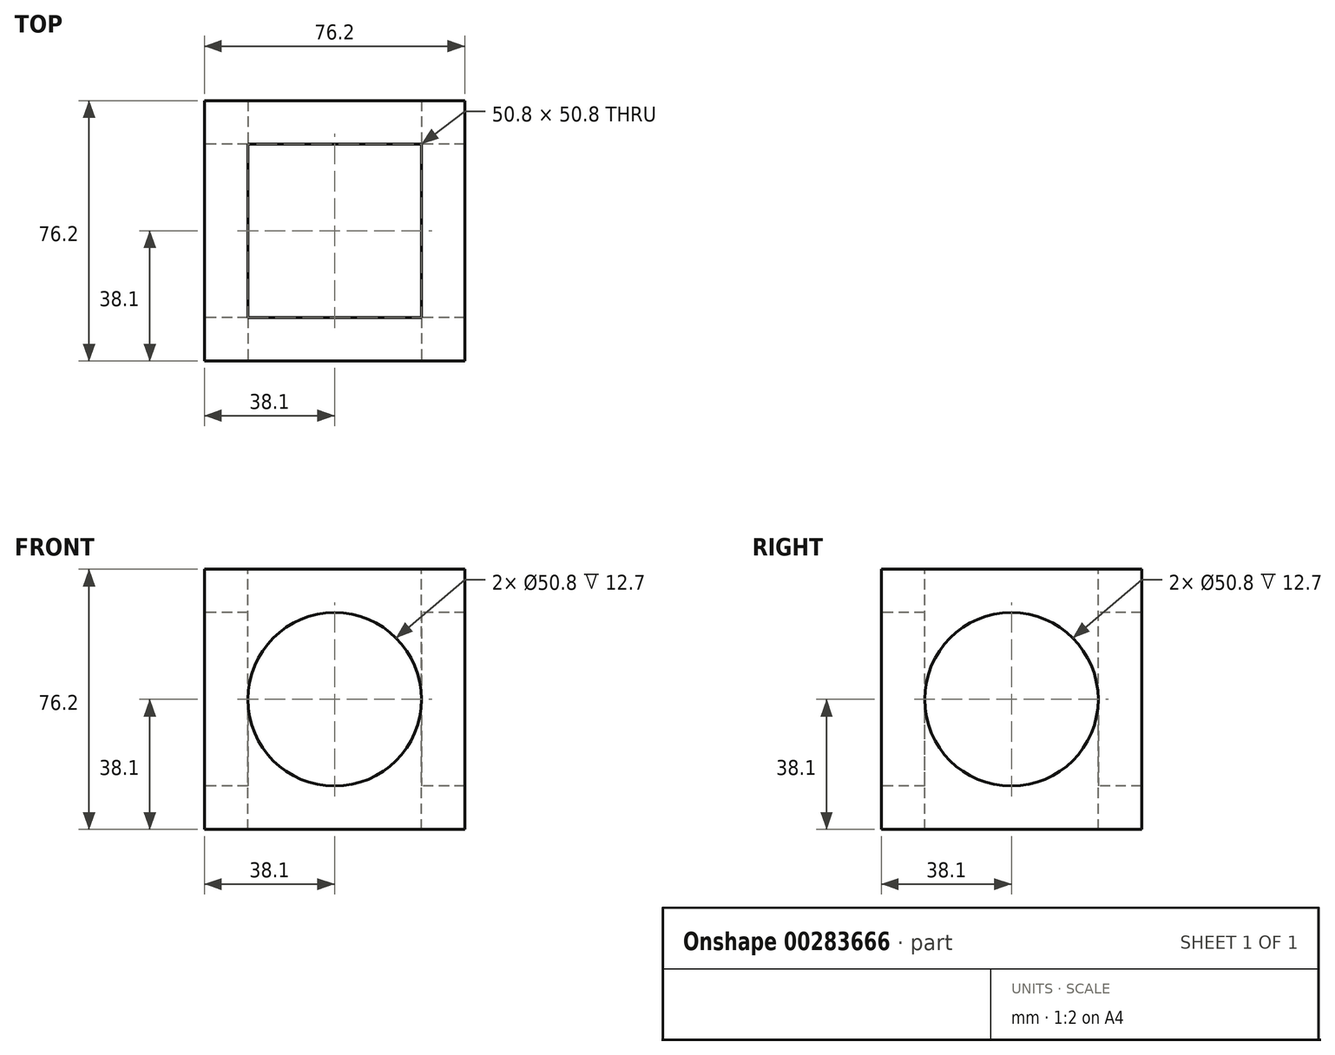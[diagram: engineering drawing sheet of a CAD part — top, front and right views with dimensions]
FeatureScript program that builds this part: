
annotation { "Feature Type Name" : "Feature", "Feature Type Description" : "" }
export const myFeature = defineFeature(function(context is Context, id is Id, definition is map)
    precondition{}
    {
        {
            var Q0;
            Q0=qCreatedBy(makeId("Front.planeOp"),FACE);
            var sketch = newSketch(context, id + "F0", { "sketchPlane" : qUnion([Q0])});
            skLineSegment(sketch, "E0.bottom", {"start": v(38.1, -38.1) * mm, "end": v(-38.1, -38.1) * mm});
            skLineSegment(sketch, "E0.top", {"start": v(38.1, 38.1) * mm, "end": v(-38.1, 38.1) * mm});
            skLineSegment(sketch, "E0.left", {"start": v(38.1, -38.1) * mm, "end": v(38.1, 38.1) * mm});
            skLineSegment(sketch, "E0.right", {"start": v(-38.1, -38.1) * mm, "end": v(-38.1, 38.1) * mm});
            skPoint(sketch, "E0.middle", {"position": v(0, 0) * mm});
            skSolve(sketch);
        }
        {
            var Q0;
            Q0 = qSketchRegion(id + "F0", true);
            extrude(context, id + "F1", {"entities" : qUnion([Q0]), "endBound" : BoundingType.SYMMETRIC, "depth" : 76.2 * mm});
        }
        {
            var Q0;
            Q0=makeQuery(id+"F1.opExtrude","CAP_FACE",FACE,{"disambiguationData":[OSD([sQuery(id+"F0.wireOp",EDGE,"E0.bottom"),sQuery(id+"F0.wireOp",EDGE,"E0.top"),sQuery(id+"F0.wireOp",EDGE,"E0.left"),sQuery(id+"F0.wireOp",EDGE,"E0.right")])],"isStart":false});
            var sketch = newSketch(context, id + "F2", { "sketchPlane" : qUnion([Q0])});
            skCircle(sketch, "E1", {"center": v(0, 0) * mm, "radius": 25.4 * mm});
            skSolve(sketch);
        }
        {
            var Q0;
            Q0=makeQuery(id+"F2.imprint","IMPRINT",FACE,{"disambiguationData":[TD([[makeQuery(id+"F2.imprint","IMPRINT",EDGE,{"derivedFrom":sQuery(id+"F2.wireOp",EDGE,"E1")}),1.0]])]});
            extrude(context, id + "F3", {"entities" : qUnion([Q0]), "operationType" : NewBodyOperationType.REMOVE, "endBound" : BoundingType.UP_TO_NEXT, "oppositeDirection" : true, "depth" : 76.2 * mm});
        }
        {
            var Q0;
            Q0=makeQuery(id+"F1.opExtrude","SWEPT_FACE",FACE,{"disambiguationData":[OSD([sQuery(id+"F0.wireOp",EDGE,"E0.right")])]});
            var sketch = newSketch(context, id + "F4", { "sketchPlane" : qUnion([Q0])});
            skCircle(sketch, "E2", {"center": v(0, 0) * mm, "radius": 25.4 * mm});
            skSolve(sketch);
        }
        {
            var Q0;
            Q0=makeQuery(id+"F4.imprint","IMPRINT",FACE,{"disambiguationData":[TD([[makeQuery(id+"F4.imprint","IMPRINT",EDGE,{"derivedFrom":sQuery(id+"F4.wireOp",EDGE,"E2")}),1.0]])]});
            extrude(context, id + "F5", {"entities" : qUnion([Q0]), "operationType" : NewBodyOperationType.REMOVE, "oppositeDirection" : true, "depth" : 76.2 * mm});
        }
        {
            var Q0;
            Q0=makeQuery(id+"F1.opExtrude","SWEPT_FACE",FACE,{"disambiguationData":[OSD([sQuery(id+"F0.wireOp",EDGE,"E0.top")])]});
            var sketch = newSketch(context, id + "F6", { "sketchPlane" : qUnion([Q0])});
            skLineSegment(sketch, "E3.bottom", {"start": v(-25.4, -25.4) * mm, "end": v(25.4, -25.4) * mm});
            skLineSegment(sketch, "E3.top", {"start": v(-25.4, 25.4) * mm, "end": v(25.4, 25.4) * mm});
            skLineSegment(sketch, "E3.left", {"start": v(-25.4, -25.4) * mm, "end": v(-25.4, 25.4) * mm});
            skLineSegment(sketch, "E3.right", {"start": v(25.4, -25.4) * mm, "end": v(25.4, 25.4) * mm});
            skPoint(sketch, "E3.middle", {"position": v(0, 0) * mm});
            skSolve(sketch);
        }
        {
            var Q0;
            Q0=makeQuery(id+"F6.imprint","IMPRINT",FACE,{"disambiguationData":[TD([[makeQuery(id+"F6.imprint","IMPRINT",EDGE,{"derivedFrom":sQuery(id+"F6.wireOp",EDGE,"E3.bottom")}),1.0]])]});
            extrude(context, id + "F7", {"entities" : qUnion([Q0]), "operationType" : NewBodyOperationType.REMOVE, "oppositeDirection" : true, "depth" : 76.2 * mm});
        }
    });
